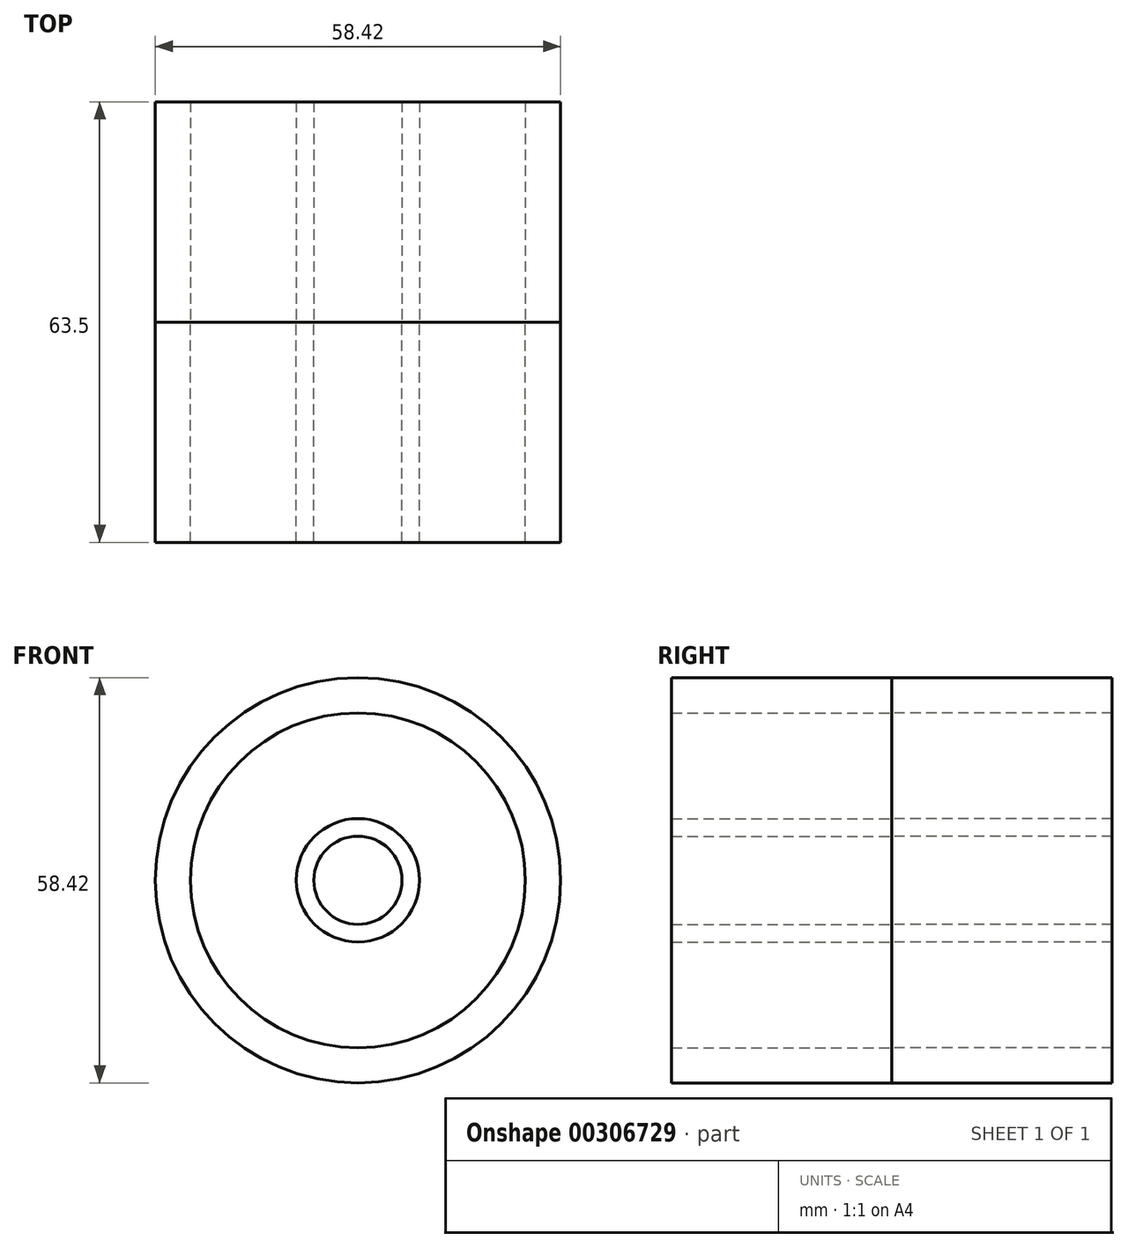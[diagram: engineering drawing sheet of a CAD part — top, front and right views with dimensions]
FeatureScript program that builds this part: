
annotation { "Feature Type Name" : "Feature", "Feature Type Description" : "" }
export const myFeature = defineFeature(function(context is Context, id is Id, definition is map)
    precondition{}
    {
        {
            var Q0;
            Q0=qCreatedBy(makeId("Front.planeOp"),FACE);
            var sketch = newSketch(context, id + "F0", { "sketchPlane" : qUnion([Q0])});
            skCircle(sketch, "E0", {"center": v(0, 0) * mm, "radius": 29.21 * mm});
            skCircle(sketch, "E1", {"center": v(0, 0) * mm, "radius": 6.35 * mm});
            skCircle(sketch, "E2", {"center": v(0, 0) * mm, "radius": 24.13 * mm});
            skCircle(sketch, "E3", {"center": v(0, 0) * mm, "radius": 8.9 * mm});
            skLineSegment(sketch, "E4", {"start": v(-1.34, -24.1) * mm, "end": v(-1.34, -8.79) * mm});
            skLineSegment(sketch, "E5", {"start": v(1.2, -24.1) * mm, "end": v(1.2, -8.8) * mm});
            skLineSegment(sketch, "E6", {"start": v(-7.8, 4.27) * mm, "end": v(-21, 11.89) * mm});
            skLineSegment(sketch, "E7", {"start": v(8.28, 3.24) * mm, "end": v(21.53, 10.89) * mm});
            skLineSegment(sketch, "E8", {"start": v(-19.63, 14.03) * mm, "end": v(-6.26, 6.31) * mm});
            skLineSegment(sketch, "E9", {"start": v(7.03, 5.45) * mm, "end": v(20.27, 13.1) * mm});
            skSolve(sketch);
        }
        {
            var Q0;
            Q0=qSketchRegion(id+"F0",true);
            extrude(context, id + "F1", {"entities" : qUnion([Q0]), "depth" : 31.75 * mm});
        }
        {
            var Q0;
            Q0=makeQuery(id+"F0.imprint","IMPRINT",FACE,{"disambiguationData":[TD([[makeQuery(id+"F0.imprint","IMPRINT",EDGE,{"derivedFrom":sQuery(id+"F0.wireOp",EDGE,"E1")}),-1.0]])]});
            extrude(context, id + "F2", {"entities" : qUnion([Q0]), "depth" : 31.75 * mm});
        }
        {
            var Q0;
            {var subQ0=sQuery(id+"F0.wireOp",EDGE,"E6");Q0=makeQuery(id+"F0.imprint","IMPRINT",FACE,{"disambiguationData":[TD([[makeQuery(id+"F0.imprint","IMPRINT",EDGE,{"derivedFrom":subQ0}),-1.0]])]});}
            var Q1;
            {var subQ0=sQuery(id+"F0.wireOp",EDGE,"E4");Q1=makeQuery(id+"F0.imprint","IMPRINT",FACE,{"disambiguationData":[TD([[makeQuery(id+"F0.imprint","IMPRINT",EDGE,{"derivedFrom":subQ0}),-1.0]])]});}
            var Q2;
            {var subQ0=sQuery(id+"F0.wireOp",EDGE,"E7");Q2=makeQuery(id+"F0.imprint","IMPRINT",FACE,{"disambiguationData":[TD([[makeQuery(id+"F0.imprint","IMPRINT",EDGE,{"derivedFrom":subQ0}),1.0]])]});}
            var Q3;
            {var subQ0=sQuery(id+"F0.wireOp",EDGE,"E4");Q3=makeQuery(id+"F0.imprint","IMPRINT",FACE,{"disambiguationData":[TD([[makeQuery(id+"F0.imprint","IMPRINT",EDGE,{"derivedFrom":subQ0}),1.0]])]});}
            var Q4;
            {var subQ0=sQuery(id+"F0.wireOp",EDGE,"E8");Q4=makeQuery(id+"F0.imprint","IMPRINT",FACE,{"disambiguationData":[TD([[makeQuery(id+"F0.imprint","IMPRINT",EDGE,{"derivedFrom":subQ0}),1.0]])]});}
            var Q5;
            {var subQ0=sQuery(id+"F0.wireOp",EDGE,"E5");Q5=makeQuery(id+"F0.imprint","IMPRINT",FACE,{"disambiguationData":[TD([[makeQuery(id+"F0.imprint","IMPRINT",EDGE,{"derivedFrom":subQ0}),-1.0]])]});}
            extrude(context, id + "F3", {"entities" : qUnion([Q0, Q1, Q2, Q3, Q4, Q5]), "depth" : 31.75 * mm});
        }
        {
            var Q0;
            Q0=makeQuery(id+"F1.opExtrude","SWEPT_BODY",BODY,{"disambiguationData":[OSD([sQuery(id+"F0.wireOp",EDGE,"E0"),sQuery(id+"F0.wireOp",EDGE,"E2")])]});
            var Q1;
            Q1=makeQuery(id+"F2.opExtrude","SWEPT_BODY",BODY,{"disambiguationData":[OSD([sQuery(id+"F0.wireOp",EDGE,"E1"),sQuery(id+"F0.wireOp",EDGE,"E3")])]});
            var Q2;
            Q2=makeQuery(id+"F3.opExtrude","SWEPT_BODY",BODY,{"disambiguationData":[OSD([sQuery(id+"F0.wireOp",EDGE,"E2"),sQuery(id+"F0.wireOp",EDGE,"E3"),sQuery(id+"F0.wireOp",EDGE,"E7"),sQuery(id+"F0.wireOp",EDGE,"E9")])]});
            var Q3;
            Q3=makeQuery(id+"F3.opExtrude","SWEPT_BODY",BODY,{"disambiguationData":[OSD([sQuery(id+"F0.wireOp",EDGE,"E2"),sQuery(id+"F0.wireOp",EDGE,"E3"),sQuery(id+"F0.wireOp",EDGE,"E6"),sQuery(id+"F0.wireOp",EDGE,"E8")])]});
            var Q4;
            Q4=makeQuery(id+"F3.opExtrude","SWEPT_BODY",BODY,{"disambiguationData":[OSD([sQuery(id+"F0.wireOp",EDGE,"E2"),sQuery(id+"F0.wireOp",EDGE,"E3"),sQuery(id+"F0.wireOp",EDGE,"E4"),sQuery(id+"F0.wireOp",EDGE,"E5")])]});
            var Q5;
            Q5=qCreatedBy(makeId("Front.planeOp"),FACE);
            mirror(context, id + "F4", {"entities" : qUnion([Q0, Q1, Q2, Q3, Q4]), "mirrorPlane" : qUnion([Q5])});
        }
    });
